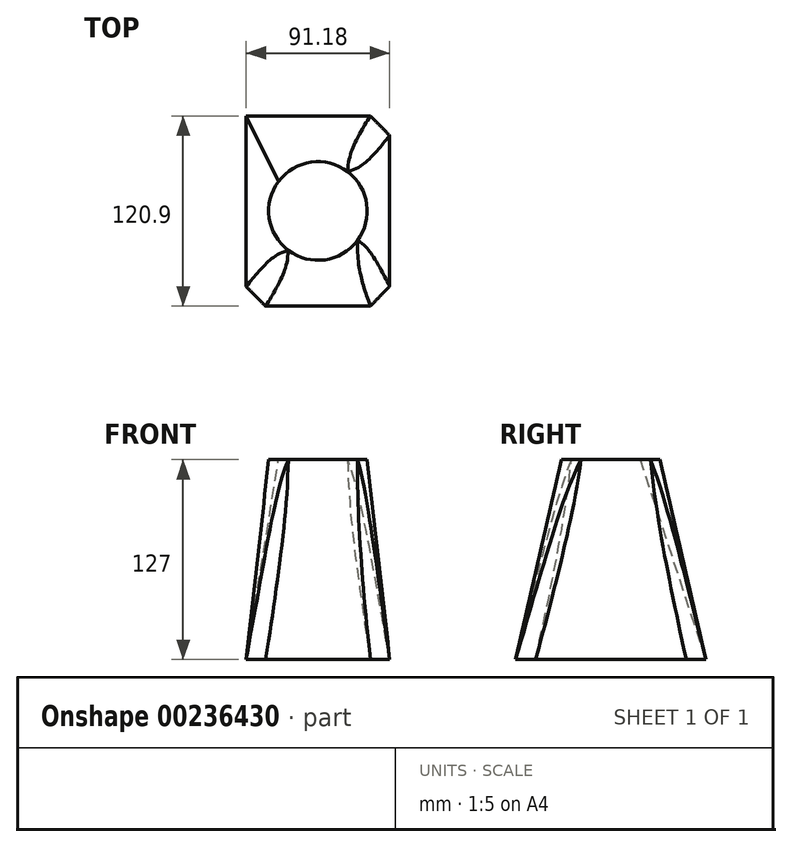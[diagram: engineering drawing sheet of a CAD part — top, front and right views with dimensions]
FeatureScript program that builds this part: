
annotation { "Feature Type Name" : "Feature", "Feature Type Description" : "" }
export const myFeature = defineFeature(function(context is Context, id is Id, definition is map)
    precondition{}
    {
        {
            var Q0;
            Q0=qCreatedBy(makeId("Top.planeOp"),FACE);
            var sketch = newSketch(context, id + "F0", { "sketchPlane" : qUnion([Q0])});
            skLineSegment(sketch, "E0.bottom", {"start": v(45.59, 60.45) * mm, "end": v(-45.59, 60.45) * mm});
            skLineSegment(sketch, "E0.top", {"start": v(45.59, -60.45) * mm, "end": v(-45.59, -60.45) * mm});
            skLineSegment(sketch, "E0.left", {"start": v(45.59, 60.45) * mm, "end": v(45.59, -60.45) * mm});
            skLineSegment(sketch, "E0.right", {"start": v(-45.59, 60.45) * mm, "end": v(-45.59, -60.45) * mm});
            skPoint(sketch, "E0.middle", {"position": v(0, 0) * mm});
            skSolve(sketch);
        }
        {
            var Q0;
            Q0=qCreatedBy(makeId("Top.planeOp"),FACE);
            cPlane(context, id + "F1", {"entities" : qUnion([Q0]), "cplaneType" : CPlaneType.OFFSET, "offset" : 127 * mm, "width" : 152.4 * mm, "height" : 152.4 * mm});
        }
        {
            var Q0;
            Q0=qCreatedBy(id+"F1.planeOp",FACE);
            var sketch = newSketch(context, id + "F2", { "sketchPlane" : qUnion([Q0])});
            skPoint(sketch, "E1.middle", {"position": v(0, 0) * mm});
            skCircle(sketch, "E2", {"center": v(0, 0) * mm, "radius": 31.3 * mm});
            skSolve(sketch);
        }
        {
            var Q0;
            Q0=makeQuery(id+"F0.imprint","IMPRINT",FACE,{"disambiguationData":[TD([[makeQuery(id+"F0.imprint","IMPRINT",EDGE,{"derivedFrom":sQuery(id+"F0.wireOp",EDGE,"E0.bottom")}),1.0]])]});
            var Q1;
            Q1=makeQuery(id+"F2.imprint","IMPRINT",FACE,{"disambiguationData":[TD([[makeQuery(id+"F2.imprint","IMPRINT",EDGE,{"derivedFrom":sQuery(id+"F2.wireOp",EDGE,"E2")}),1.0]])]});
            loft(context, id + "F3", {"sheetProfilesArray" : [{ "sheetProfileEntities" : qUnion([Q0]) }, { "sheetProfileEntities" : qUnion([Q1]) }]});
        }
        {
            var Q0;
            Q0=makeQuery(id+"F3.opLoft","SWEPT_EDGE",EDGE,{"disambiguationData":[OSD([sQuery(id+"F0.wireOp",EDGE,"E0.top"),sQuery(id+"F0.wireOp",EDGE,"E0.left"),sQuery(id+"F0.wireOp",EDGE,"E0.right"),sQuery(id+"F2.wireOp",EDGE,"E2")])]});
            var Q1;
            Q1=makeQuery(id+"F3.opLoft","SWEPT_EDGE",EDGE,{"disambiguationData":[OSD([sQuery(id+"F0.wireOp",EDGE,"E0.bottom"),sQuery(id+"F0.wireOp",EDGE,"E0.left")])]});
            var Q2;
            Q2=makeQuery(id+"F3.opLoft","SWEPT_EDGE",EDGE,{"disambiguationData":[OSD([sQuery(id+"F0.wireOp",EDGE,"E0.bottom"),sQuery(id+"F0.wireOp",EDGE,"E0.left"),sQuery(id+"F0.wireOp",EDGE,"E0.right"),sQuery(id+"F2.wireOp",EDGE,"E2")])]});
            var Q3;
            Q3=makeQuery(id+"F3.opLoft","SWEPT_EDGE",EDGE,{"disambiguationData":[OSD([sQuery(id+"F0.wireOp",EDGE,"E0.bottom"),sQuery(id+"F0.wireOp",EDGE,"E0.top"),sQuery(id+"F0.wireOp",EDGE,"E0.right"),sQuery(id+"F2.wireOp",EDGE,"E2")])]});
            chamfer(context, id + "F4", {"entities" : qUnion([Q0, Q1, Q2, Q3]), "width" : 12.7 * mm, "tangentPropagation" : true});
        }
    });
